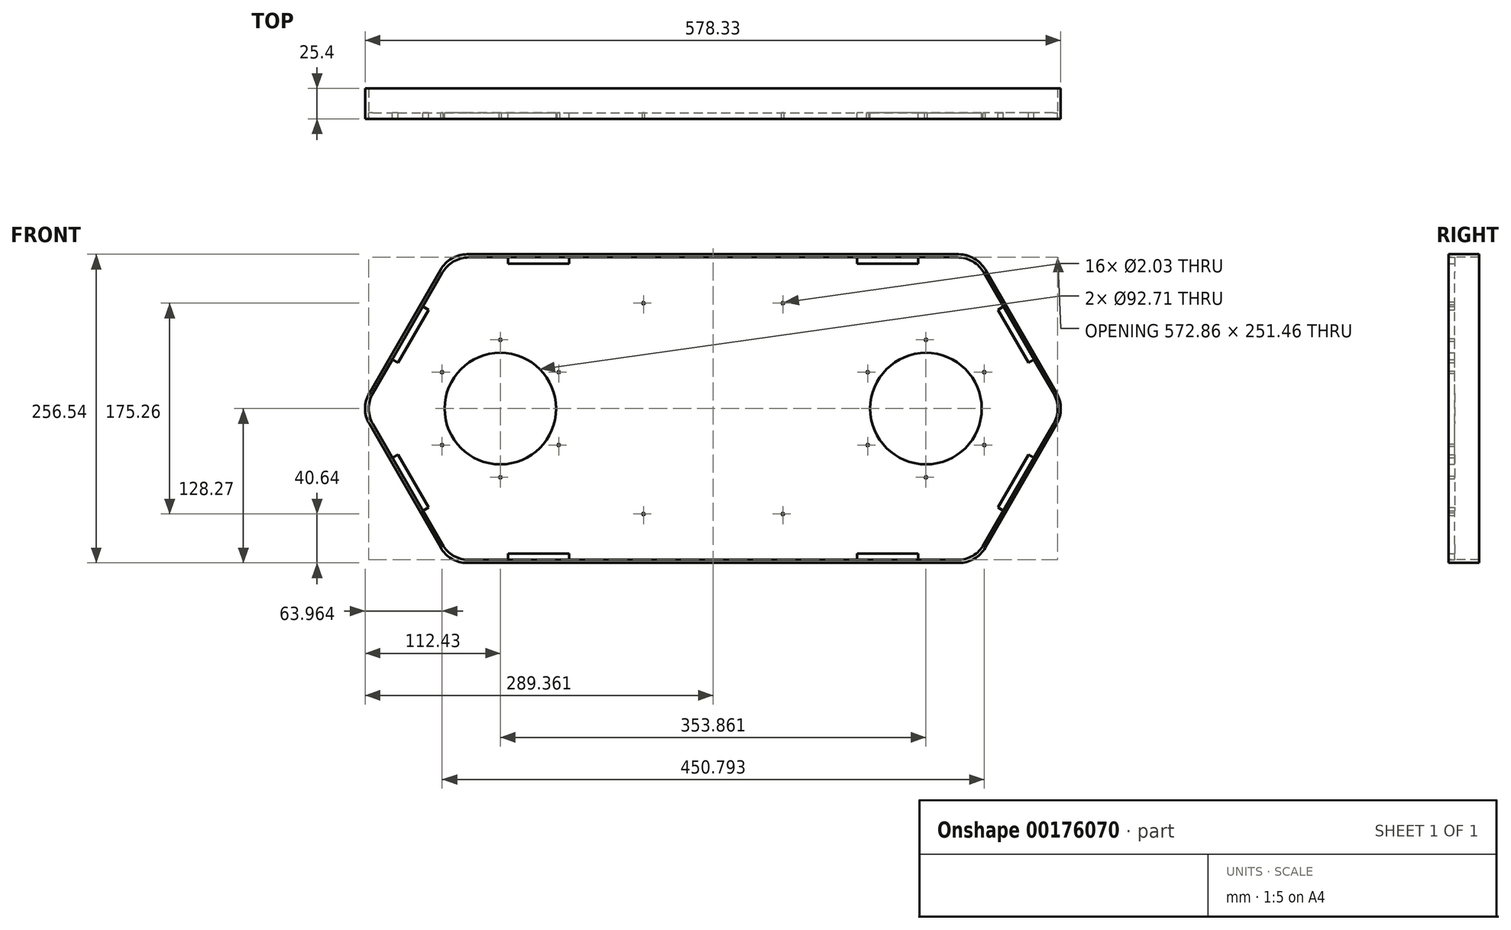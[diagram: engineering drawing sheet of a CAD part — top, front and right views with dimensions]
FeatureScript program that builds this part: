
annotation { "Feature Type Name" : "Feature", "Feature Type Description" : "" }
export const myFeature = defineFeature(function(context is Context, id is Id, definition is map)
    precondition{}
    {
        {
            var Q0;
            Q0=qCreatedBy(makeId("Front.planeOp"),FACE);
            var sketch = newSketch(context, id + "F0", { "sketchPlane" : qUnion([Q0])});
            skCircle(sketch, "E0.cCircle", {"center": v(0, 0) * mm, "radius": 125.73 * mm, "construction": true});
            skLineSegment(sketch, "E0.0", {"start": v(72.6, 125.73) * mm, "end": v(145.18, 0) * mm, "construction": true});
            skLineSegment(sketch, "E0.1", {"start": v(145.18, 0) * mm, "end": v(72.6, -125.73) * mm, "construction": true});
            skLineSegment(sketch, "E0.2", {"start": v(72.6, -125.73) * mm, "end": v(-72.6, -125.73) * mm, "construction": true});
            skLineSegment(sketch, "E0.3", {"start": v(-72.6, -125.73) * mm, "end": v(-145.18, 0) * mm, "construction": true});
            skLineSegment(sketch, "E0.4", {"start": v(-145.18, 0) * mm, "end": v(-72.6, 125.73) * mm, "construction": true});
            skLineSegment(sketch, "E0.5", {"start": v(-72.6, 125.73) * mm, "end": v(72.6, 125.73) * mm, "construction": true});
            skPoint(sketch, "E0.0.midPoint", {"position": v(108.89, 62.86) * mm});
            skCircle(sketch, "E1.cCircle", {"center": v(290.36, 0) * mm, "radius": 125.73 * mm, "construction": true});
            skLineSegment(sketch, "E1.0", {"start": v(362.95, 125.73) * mm, "end": v(435.54, 0) * mm, "construction": true});
            skLineSegment(sketch, "E1.1", {"start": v(435.54, 0) * mm, "end": v(362.95, -125.73) * mm, "construction": true});
            skLineSegment(sketch, "E1.2", {"start": v(362.95, -125.73) * mm, "end": v(217.77, -125.73) * mm, "construction": true});
            skLineSegment(sketch, "E1.3", {"start": v(217.77, -125.73) * mm, "end": v(145.18, 0) * mm, "construction": true});
            skLineSegment(sketch, "E1.4", {"start": v(145.18, 0) * mm, "end": v(217.77, 125.73) * mm, "construction": true});
            skLineSegment(sketch, "E1.5", {"start": v(217.77, 125.73) * mm, "end": v(362.95, 125.73) * mm, "construction": true});
            skPoint(sketch, "E1.0.midPoint", {"position": v(399.25, 62.86) * mm});
            skLineSegment(sketch, "E2", {"start": v(72.6, 125.73) * mm, "end": v(217.77, 125.73) * mm});
            skLineSegment(sketch, "E3", {"start": v(217.77, -125.73) * mm, "end": v(72.6, -125.73) * mm});
            skLineSegment(sketch, "E4", {"start": v(72.6, -125.73) * mm, "end": v(-57.93, -125.73) * mm});
            skLineSegment(sketch, "E5", {"start": v(-79.92, -113.03) * mm, "end": v(-137.85, -12.7) * mm});
            skLineSegment(sketch, "E6", {"start": v(-137.85, 12.7) * mm, "end": v(-79.92, 113.03) * mm});
            skLineSegment(sketch, "E7", {"start": v(-57.93, 125.73) * mm, "end": v(72.6, 125.73) * mm});
            skLineSegment(sketch, "E8", {"start": v(217.77, 125.73) * mm, "end": v(348.29, 125.73) * mm});
            skLineSegment(sketch, "E9", {"start": v(370.28, 113.03) * mm, "end": v(428.2, 12.7) * mm});
            skLineSegment(sketch, "E10", {"start": v(428.2, -12.7) * mm, "end": v(370.28, -113.03) * mm});
            skLineSegment(sketch, "E11", {"start": v(348.29, -125.73) * mm, "end": v(217.77, -125.73) * mm});
            skPoint(sketch, "E12.visualSharp", {"position": v(-72.6, 125.73) * mm});
            skArc(sketch, "E12.filletArc", {"start": v(-57.93, 125.73) * mm, "mid": v(-70.63, 122.33) * mm, "end": v(-79.92, 113.03) * mm});
            skPoint(sketch, "E13.visualSharp", {"position": v(-145.18, 0) * mm});
            skArc(sketch, "E13.filletArc", {"start": v(-137.85, 12.7) * mm, "mid": v(-141.25, 0) * mm, "end": v(-137.85, -12.7) * mm});
            skPoint(sketch, "E14.visualSharp", {"position": v(-72.6, -125.73) * mm});
            skArc(sketch, "E14.filletArc", {"start": v(-79.92, -113.03) * mm, "mid": v(-70.63, -122.33) * mm, "end": v(-57.93, -125.73) * mm});
            skPoint(sketch, "E15.visualSharp", {"position": v(362.95, -125.73) * mm});
            skArc(sketch, "E15.filletArc", {"start": v(348.29, -125.73) * mm, "mid": v(360.99, -122.33) * mm, "end": v(370.28, -113.03) * mm});
            skPoint(sketch, "E16.visualSharp", {"position": v(435.54, 0) * mm});
            skArc(sketch, "E16.filletArc", {"start": v(428.2, -12.7) * mm, "mid": v(431.61, 0) * mm, "end": v(428.2, 12.7) * mm});
            skPoint(sketch, "E17.visualSharp", {"position": v(362.95, 125.73) * mm});
            skArc(sketch, "E17.filletArc", {"start": v(370.28, 113.03) * mm, "mid": v(360.99, 122.33) * mm, "end": v(348.29, 125.73) * mm});
            skCircle(sketch, "E18", {"center": v(145.18, 0) * mm, "radius": 46.35 * mm, "construction": true});
            skLineSegment(sketch, "E19", {"start": v(145.18, 0) * mm, "end": v(145.18, 139.98) * mm, "construction": true});
            skPoint(sketch, "E19.endSnap0", {"position": v(145.18, 125.73) * mm});
            skLineSegment(sketch, "E20.bottom", {"start": v(-25.4, 125.73) * mm, "end": v(25.4, 125.73) * mm});
            skLineSegment(sketch, "E20.top", {"start": v(-25.4, 120.4) * mm, "end": v(25.4, 120.4) * mm});
            skLineSegment(sketch, "E20.left", {"start": v(-25.4, 125.73) * mm, "end": v(-25.4, 120.4) * mm});
            skLineSegment(sketch, "E20.right", {"start": v(25.4, 125.73) * mm, "end": v(25.4, 120.4) * mm});
            skLineSegment(sketch, "E21.bottom", {"start": v(-25.4, -125.73) * mm, "end": v(25.4, -125.73) * mm});
            skLineSegment(sketch, "E21.top", {"start": v(-25.4, -120.4) * mm, "end": v(25.4, -120.4) * mm});
            skLineSegment(sketch, "E21.left", {"start": v(-25.4, -125.73) * mm, "end": v(-25.4, -120.4) * mm});
            skLineSegment(sketch, "E21.right", {"start": v(25.4, -125.73) * mm, "end": v(25.4, -120.4) * mm});
            skPoint(sketch, "E22", {"position": v(0, 120.4) * mm});
            skPoint(sketch, "E23", {"position": v(0, -120.4) * mm});
            skLineSegment(sketch, "E24", {"start": v(-121.59, -40.87) * mm, "end": v(-116.97, -38.2) * mm});
            skLineSegment(sketch, "E25", {"start": v(-116.97, -38.2) * mm, "end": v(-91.57, -82.2) * mm});
            skPoint(sketch, "E26", {"position": v(-104.27, -60.2) * mm});
            skPoint(sketch, "E27", {"position": v(-108.89, 62.86) * mm});
            skPoint(sketch, "E28", {"position": v(-108.89, -62.86) * mm});
            skLineSegment(sketch, "E29", {"start": v(-108.89, -62.86) * mm, "end": v(-104.27, -60.2) * mm, "construction": true});
            skLineSegment(sketch, "E30", {"start": v(-91.57, -82.2) * mm, "end": v(-96.19, -84.86) * mm});
            skLineSegment(sketch, "E31", {"start": v(-116.97, 38.2) * mm, "end": v(-91.57, 82.2) * mm});
            skLineSegment(sketch, "E32", {"start": v(-91.57, 82.2) * mm, "end": v(-97.07, 85.37) * mm});
            skLineSegment(sketch, "E33", {"start": v(-116.97, 38.2) * mm, "end": v(-121.59, 40.87) * mm});
            skPoint(sketch, "E34", {"position": v(-104.27, 60.2) * mm});
            skLineSegment(sketch, "E35", {"start": v(-104.27, 60.2) * mm, "end": v(-122.63, 70.8) * mm, "construction": true});
            skLineSegment(sketch, "E36.MirrorCS", {"start": v(264.96, -125.73) * mm, "end": v(264.96, -120.4) * mm});
            skLineSegment(sketch, "E37.MirrorCS", {"start": v(315.76, -125.73) * mm, "end": v(315.76, -120.4) * mm});
            skLineSegment(sketch, "E38.MirrorCS", {"start": v(315.76, -120.4) * mm, "end": v(264.96, -120.4) * mm});
            skLineSegment(sketch, "E39.MirrorCS", {"start": v(381.93, -82.2) * mm, "end": v(386.55, -84.86) * mm});
            skLineSegment(sketch, "E40.MirrorCS", {"start": v(407.33, -38.2) * mm, "end": v(381.93, -82.2) * mm});
            skLineSegment(sketch, "E41.MirrorCS", {"start": v(411.95, -40.87) * mm, "end": v(407.33, -38.2) * mm});
            skLineSegment(sketch, "E42.MirrorCS", {"start": v(407.33, 38.2) * mm, "end": v(411.95, 40.87) * mm});
            skLineSegment(sketch, "E43.MirrorCS", {"start": v(407.33, 38.2) * mm, "end": v(381.93, 82.2) * mm});
            skLineSegment(sketch, "E44.MirrorCS", {"start": v(381.93, 82.2) * mm, "end": v(387.43, 85.37) * mm});
            skLineSegment(sketch, "E45.MirrorCS", {"start": v(264.96, 125.73) * mm, "end": v(264.96, 120.4) * mm});
            skLineSegment(sketch, "E46.MirrorCS", {"start": v(315.76, 125.73) * mm, "end": v(315.76, 120.4) * mm});
            skLineSegment(sketch, "E47.MirrorCS", {"start": v(315.76, 120.4) * mm, "end": v(264.96, 120.4) * mm});
            skCircle(sketch, "E48", {"center": v(-31.75, 0) * mm, "radius": 46.35 * mm});
            skCircle(sketch, "E49", {"center": v(322.11, 0) * mm, "radius": 46.35 * mm});
            skCircle(sketch, "E50", {"center": v(-31.75, 0) * mm, "radius": 57.15 * mm, "construction": true});
            skCircle(sketch, "E51", {"center": v(-31.75, 57.15) * mm, "radius": 1.02 * mm});
            skCircle(sketch, "E52", {"center": v(16.72, 30.28) * mm, "radius": 1.02 * mm});
            skCircle(sketch, "E53", {"center": v(-80.22, 30.28) * mm, "radius": 1.02 * mm});
            skLineSegment(sketch, "E54", {"start": v(145.18, 0) * mm, "end": v(157.43, 0) * mm, "construction": true});
            skLineSegment(sketch, "E55", {"start": v(-31.75, 0) * mm, "end": v(-31.75, 57.15) * mm, "construction": true});
            skLineSegment(sketch, "E56", {"start": v(-31.75, 0) * mm, "end": v(16.72, 30.28) * mm, "construction": true});
            skLineSegment(sketch, "E57", {"start": v(-31.75, 0) * mm, "end": v(-80.22, 30.28) * mm, "construction": true});
            skCircle(sketch, "E58.MirrorC", {"center": v(16.72, -30.28) * mm, "radius": 1.02 * mm});
            skCircle(sketch, "E59.MirrorC", {"center": v(-31.75, -57.15) * mm, "radius": 1.02 * mm});
            skCircle(sketch, "E60.MirrorC", {"center": v(-80.22, -30.28) * mm, "radius": 1.02 * mm});
            skCircle(sketch, "E61.MirrorC", {"center": v(273.65, -30.28) * mm, "radius": 1.02 * mm});
            skCircle(sketch, "E62.MirrorC", {"center": v(322.11, -57.15) * mm, "radius": 1.02 * mm});
            skCircle(sketch, "E63.MirrorC", {"center": v(370.58, -30.28) * mm, "radius": 1.02 * mm});
            skCircle(sketch, "E64.MirrorC", {"center": v(370.58, 30.28) * mm, "radius": 1.02 * mm});
            skCircle(sketch, "E65.MirrorC", {"center": v(273.65, 30.28) * mm, "radius": 1.02 * mm});
            skCircle(sketch, "E66.MirrorC", {"center": v(322.11, 57.15) * mm, "radius": 1.02 * mm});
            skCircle(sketch, "E67.MirrorC", {"center": v(87.24, -87.63) * mm, "radius": 1.02 * mm});
            skCircle(sketch, "E68.MirrorC", {"center": v(87.24, 87.63) * mm, "radius": 1.02 * mm});
            skCircle(sketch, "E69.MirrorC", {"center": v(203.12, -87.63) * mm, "radius": 1.02 * mm});
            skCircle(sketch, "E70.MirrorC", {"center": v(203.12, 87.63) * mm, "radius": 1.02 * mm});
            skSolve(sketch);
        }
        {
            var Q0;
            Q0=makeQuery(id+"F0.imprint","IMPRINT",FACE,{"disambiguationData":[TD([[makeQuery(id+"F0.imprint","IMPRINT",EDGE,{"derivedFrom":sQuery(id+"F0.wireOp",EDGE,"E4")}),-1.0]])]});
            extrude(context, id + "F1", {"entities" : qUnion([Q0]), "depth" : 5.08 * mm});
        }
        {
            var Q0;
            Q0=makeQuery(id+"F1.opExtrude","CAP_FACE",FACE,{"disambiguationData":[OSD([sQuery(id+"F0.wireOp",EDGE,"E2"),sQuery(id+"F0.wireOp",EDGE,"E3"),sQuery(id+"F0.wireOp",EDGE,"E4"),sQuery(id+"F0.wireOp",EDGE,"E5"),sQuery(id+"F0.wireOp",EDGE,"E6"),sQuery(id+"F0.wireOp",EDGE,"E7"),sQuery(id+"F0.wireOp",EDGE,"E8"),sQuery(id+"F0.wireOp",EDGE,"E9"),sQuery(id+"F0.wireOp",EDGE,"E10"),sQuery(id+"F0.wireOp",EDGE,"E11"),sQuery(id+"F0.wireOp",EDGE,"E12.filletArc"),sQuery(id+"F0.wireOp",EDGE,"E13.filletArc"),sQuery(id+"F0.wireOp",EDGE,"E14.filletArc"),sQuery(id+"F0.wireOp",EDGE,"E15.filletArc"),sQuery(id+"F0.wireOp",EDGE,"E16.filletArc"),sQuery(id+"F0.wireOp",EDGE,"E17.filletArc"),sQuery(id+"F0.wireOp",EDGE,"E20.top"),sQuery(id+"F0.wireOp",EDGE,"E20.left"),sQuery(id+"F0.wireOp",EDGE,"E20.right"),sQuery(id+"F0.wireOp",EDGE,"E21.top"),sQuery(id+"F0.wireOp",EDGE,"E21.left"),sQuery(id+"F0.wireOp",EDGE,"E21.right"),sQuery(id+"F0.wireOp",EDGE,"E24"),sQuery(id+"F0.wireOp",EDGE,"E25"),sQuery(id+"F0.wireOp",EDGE,"E30"),sQuery(id+"F0.wireOp",EDGE,"E31"),sQuery(id+"F0.wireOp",EDGE,"E32"),sQuery(id+"F0.wireOp",EDGE,"E33"),sQuery(id+"F0.wireOp",EDGE,"E36.MirrorCS"),sQuery(id+"F0.wireOp",EDGE,"E37.MirrorCS"),sQuery(id+"F0.wireOp",EDGE,"E38.MirrorCS"),sQuery(id+"F0.wireOp",EDGE,"E39.MirrorCS"),sQuery(id+"F0.wireOp",EDGE,"E40.MirrorCS"),sQuery(id+"F0.wireOp",EDGE,"E41.MirrorCS"),sQuery(id+"F0.wireOp",EDGE,"E42.MirrorCS"),sQuery(id+"F0.wireOp",EDGE,"E43.MirrorCS"),sQuery(id+"F0.wireOp",EDGE,"E44.MirrorCS"),sQuery(id+"F0.wireOp",EDGE,"E45.MirrorCS"),sQuery(id+"F0.wireOp",EDGE,"E46.MirrorCS"),sQuery(id+"F0.wireOp",EDGE,"E47.MirrorCS"),sQuery(id+"F0.wireOp",EDGE,"E48"),sQuery(id+"F0.wireOp",EDGE,"E49"),sQuery(id+"F0.wireOp",EDGE,"E51"),sQuery(id+"F0.wireOp",EDGE,"E52"),sQuery(id+"F0.wireOp",EDGE,"E53"),sQuery(id+"F0.wireOp",EDGE,"E58.MirrorC"),sQuery(id+"F0.wireOp",EDGE,"E59.MirrorC"),sQuery(id+"F0.wireOp",EDGE,"E60.MirrorC"),sQuery(id+"F0.wireOp",EDGE,"E61.MirrorC"),sQuery(id+"F0.wireOp",EDGE,"E62.MirrorC"),sQuery(id+"F0.wireOp",EDGE,"E63.MirrorC"),sQuery(id+"F0.wireOp",EDGE,"E64.MirrorC"),sQuery(id+"F0.wireOp",EDGE,"E65.MirrorC"),sQuery(id+"F0.wireOp",EDGE,"E66.MirrorC"),sQuery(id+"F0.wireOp",EDGE,"E67.MirrorC"),sQuery(id+"F0.wireOp",EDGE,"E68.MirrorC"),sQuery(id+"F0.wireOp",EDGE,"E69.MirrorC"),sQuery(id+"F0.wireOp",EDGE,"E70.MirrorC")])],"isStart":false});
            var sketch = newSketch(context, id + "F2", { "sketchPlane" : qUnion([Q0])});
            skPoint(sketch, "E71", {"position": v(145.18, 125.73) * mm});
            skCircle(sketch, "E72.cCircle", {"center": v(0, 0) * mm, "radius": 128.27 * mm, "construction": true});
            skLineSegment(sketch, "E72.0", {"start": v(-59.4, 128.27) * mm, "end": v(74.06, 128.27) * mm});
            skLineSegment(sketch, "E72.3", {"start": v(74.06, -128.27) * mm, "end": v(-59.4, -128.27) * mm});
            skLineSegment(sketch, "E72.4", {"start": v(-81.39, -115.57) * mm, "end": v(-140.78, -12.7) * mm});
            skLineSegment(sketch, "E72.5", {"start": v(-140.78, 12.7) * mm, "end": v(-81.39, 115.57) * mm});
            skPoint(sketch, "E72.0.midPoint", {"position": v(0, 128.27) * mm});
            skPoint(sketch, "E73.visualSharp", {"position": v(-74.06, 128.27) * mm});
            skArc(sketch, "E73.filletArc", {"start": v(-59.4, 128.27) * mm, "mid": v(-72.1, 124.87) * mm, "end": v(-81.39, 115.57) * mm});
            skPoint(sketch, "E74.visualSharp", {"position": v(-148.11, 0) * mm});
            skArc(sketch, "E74.filletArc", {"start": v(-140.78, 12.7) * mm, "mid": v(-144.18, 0) * mm, "end": v(-140.78, -12.7) * mm});
            skPoint(sketch, "E75.visualSharp", {"position": v(-74.06, -128.27) * mm});
            skArc(sketch, "E75.filletArc", {"start": v(-81.39, -115.57) * mm, "mid": v(-72.1, -124.87) * mm, "end": v(-59.4, -128.27) * mm});
            skCircle(sketch, "E76.cCircle", {"center": v(289.97, 0) * mm, "radius": 128.27 * mm, "construction": true});
            skLineSegment(sketch, "E76.0", {"start": v(215.91, 128.27) * mm, "end": v(349.36, 128.27) * mm});
            skLineSegment(sketch, "E76.1", {"start": v(371.36, 115.57) * mm, "end": v(430.75, 12.7) * mm});
            skLineSegment(sketch, "E76.2", {"start": v(430.75, -12.7) * mm, "end": v(371.36, -115.57) * mm});
            skLineSegment(sketch, "E76.3", {"start": v(425.87, -128.27) * mm, "end": v(349.36, -128.27) * mm});
            skPoint(sketch, "E76.0.midPoint", {"position": v(289.97, 128.27) * mm});
            skPoint(sketch, "E77.visualSharp", {"position": v(364.02, 128.27) * mm});
            skArc(sketch, "E77.filletArc", {"start": v(371.36, 115.57) * mm, "mid": v(362.06, 124.87) * mm, "end": v(349.36, 128.27) * mm});
            skPoint(sketch, "E78.visualSharp", {"position": v(438.08, 0) * mm});
            skArc(sketch, "E78.filletArc", {"start": v(430.75, -12.7) * mm, "mid": v(434.15, 0) * mm, "end": v(430.75, 12.7) * mm});
            skPoint(sketch, "E79.visualSharp", {"position": v(364.02, -128.27) * mm});
            skArc(sketch, "E79.filletArc", {"start": v(349.36, -128.27) * mm, "mid": v(362.06, -124.87) * mm, "end": v(371.36, -115.57) * mm});
            skPoint(sketch, "E80", {"position": v(434.15, 0) * mm});
            skLineSegment(sketch, "E81", {"start": v(74.06, 128.27) * mm, "end": v(215.91, 128.27) * mm});
            skLineSegment(sketch, "E82", {"start": v(349.36, -128.27) * mm, "end": v(74.06, -128.27) * mm});
            skLineSegment(sketch, "E83", {"start": v(-25.4, 125.73) * mm, "end": v(25.4, 125.73) * mm});
            skLineSegment(sketch, "E84", {"start": v(-96.19, 84.86) * mm, "end": v(-121.59, 40.87) * mm});
            skLineSegment(sketch, "E85", {"start": v(-121.59, -40.87) * mm, "end": v(-96.19, -84.86) * mm});
            skLineSegment(sketch, "E86", {"start": v(-25.4, -125.73) * mm, "end": v(25.4, -125.73) * mm});
            skLineSegment(sketch, "E87", {"start": v(264.96, -125.73) * mm, "end": v(315.76, -125.73) * mm});
            skLineSegment(sketch, "E88", {"start": v(386.55, -84.86) * mm, "end": v(411.95, -40.87) * mm});
            skLineSegment(sketch, "E89", {"start": v(411.95, 40.87) * mm, "end": v(386.55, 84.86) * mm});
            skLineSegment(sketch, "E90", {"start": v(315.76, 125.73) * mm, "end": v(264.96, 125.73) * mm});
            skSolve(sketch);
        }
        {
            var Q0;
            Q0=makeQuery(id+"F2.imprint","IMPRINT",FACE,{"disambiguationData":[TD([[makeQuery(id+"F2.imprint","IMPRINT",EDGE,{"derivedFrom":sQuery(id+"F2.wireOp",EDGE,"E72.0")}),-1.0]])]});
            extrude(context, id + "F3", {"entities" : qUnion([Q0]), "oppositeDirection" : true, "depth" : 25.4 * mm});
        }
    });
